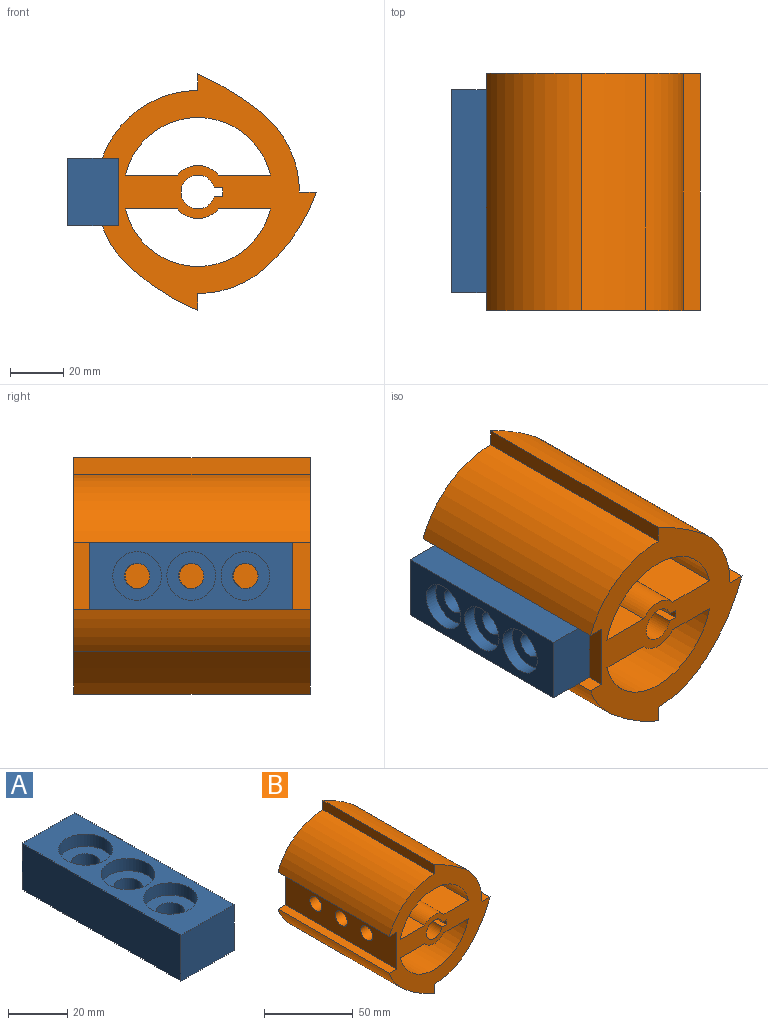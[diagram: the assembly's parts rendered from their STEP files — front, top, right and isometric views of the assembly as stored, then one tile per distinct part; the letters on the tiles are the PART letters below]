
ASSEMBLY  parts=2 mates=1
PART A: 15 faces, bbox 25.4x76.2x19.1 mm
  f0: cylinder r=4.76mm len=13.97mm, axis (0,0,1), area 418mm2, adj f5,f14
  f1: cylinder r=4.76mm len=13.97mm, axis (0,0,1), area 418mm2, adj f5,f12
  f2: cylinder r=4.76mm len=13.97mm, axis (0,0,1), area 418mm2, adj f5,f10
  f3: plane 76.2x25.4mm, normal (0,0,1), area 1147.4mm2, adj f4,f6,f7,f8,f9,f11,f13
  f4: plane 76.2x19.05mm, normal (-1,0,0), area 1451.6mm2, adj f3,f5,f7,f8
  f5: plane 76.2x25.4mm, normal (0,0,-1), area 1721.7mm2, adj f0,f1,f2,f4,f6,f7,f8
  f6: plane 76.2x19.05mm, normal (1,0,0), area 1451.6mm2, adj f3,f5,f7,f8
  f7: plane 25.4x19.05mm, normal (0,1,0), area 483.9mm2, adj f3,f4,f5,f6
  f8: plane 25.4x19.05mm, normal (0,-1,0), area 483.9mm2, adj f3,f4,f5,f6
  f9: cylinder r=9.14mm len=18.29mm, axis (0,0,1), area 291.9mm2, adj f3,f10
  f10: plane 18.29x18.29mm, normal (0,0,1), area 191.4mm2, adj f2,f9
  f11: cylinder r=9.14mm len=18.29mm, axis (0,0,1), area 291.9mm2, adj f3,f12
  f12: plane 18.29x18.29mm, normal (0,0,1), area 191.4mm2, adj f1,f11
  f13: cylinder r=9.14mm len=18.29mm, axis (0,0,1), area 291.9mm2, adj f3,f14
  f14: plane 18.29x18.29mm, normal (0,0,1), area 191.4mm2, adj f0,f13
PART B: 33 faces, bbox 80.4x88.9x88.9 mm
  f0: cylinder r=38.1mm len=88.9mm, axis (0,1,0), area 1702.8mm2, adj f1,f2,f14,f24
  f1: plane 88.9x80.37mm, normal (0,-1,0), area 2746.6mm2, adj f0,f3,f4,f5,f6,f7,f8,f9
  f2: plane 88.9x80.37mm, normal (0,1,0), area 2746.6mm2, adj f0,f3,f4,f5,f6,f7,f8,f9
  f3: cylinder r=6.35mm len=88.9mm, axis (0,1,0), area 3261.7mm2, adj f1,f2,f4,f23
  f4: plane 88.9x3.24mm, normal (0,0,-1), area 288.3mm2, adj f1,f2,f3,f5
  f5: plane 88.9x3.18mm, normal (-1,0,0), area 282.3mm2, adj f1,f2,f4,f23
  f6: cylinder r=9.97mm len=88.9mm, axis (0,1,0), area 1561.5mm2, adj f1,f2,f7,f20
  f7: plane 88.9x19.52mm, normal (0,0,-1), area 1735.2mm2, adj f1,f2,f6,f8
  f8: cylinder r=27.94mm len=88.9mm, axis (0,1,0), area 6664.3mm2, adj f1,f2,f7,f20
  f9: plane 88.9x19.52mm, normal (0,0,1), area 1735.2mm2, adj f1,f2,f10,f21
  f10: cylinder r=9.97mm len=88.9mm, axis (0,1,0), area 1561.5mm2, adj f1,f2,f9,f11
  f11: plane 88.9x19.52mm, normal (0,0,1), area 1735.2mm2, adj f1,f2,f10,f21
  f12: plane 88.9x6.35mm, normal (-1,0,0), area 564.5mm2, adj f1,f2,f13,f22
  f13: cylinder r=38.1mm len=88.9mm, axis (0,1,0), area 4169.4mm2, adj f1,f2,f12,f26
  f14: cylinder r=91.33mm len=88.9mm, axis (0,1,0), area 2678.3mm2, adj f0,f1,f2,f15
  f15: plane 88.9x6.35mm, normal (1,0,0), area 564.5mm2, adj f1,f2,f14,f16
  f16: cylinder r=38.1mm len=88.9mm, axis (0,1,0), area 2429.9mm2, adj f1,f2,f15,f17
  f17: cylinder r=67.63mm len=88.9mm, axis (0,1,0), area 3115.1mm2, adj f1,f2,f16,f18
  f18: plane 88.9x6.35mm, normal (0,0,1), area 564.5mm2, adj f1,f2,f17,f19
  f19: cylinder r=38.1mm len=88.9mm, axis (0,1,0), area 3045.6mm2, adj f1,f2,f18,f22
  f20: plane 88.9x19.52mm, normal (0,0,-1), area 1735.2mm2, adj f1,f2,f6,f8
  f21: cylinder r=27.94mm len=88.9mm, axis (0,1,0), area 6664.3mm2, adj f1,f2,f9,f11
  f22: cylinder r=117.44mm len=88.9mm, axis (0,1,0), area 2482.2mm2, adj f1,f2,f12,f19
  f23: plane 88.9x3.24mm, normal (0,0,1), area 288.3mm2, adj f1,f2,f3,f5
  f24: plane 88.9x6.08mm, normal (0,0,1), area 540.2mm2, adj f0,f1,f2,f25
  f25: plane 88.9x25.4mm, normal (-1,0,0), area 2044.3mm2, adj f1,f2,f24,f26,f27,f29,f31
  f26: plane 88.9x6.08mm, normal (0,0,-1), area 540.2mm2, adj f1,f2,f13,f25
  f27: cylinder r=4.76mm len=12.7mm, axis (-1,0,0), area 380mm2, adj f25,f28
  f28: plane 9.53x9.53mm, normal (-1,0,0), area 71.3mm2, adj f27
  f29: cylinder r=4.76mm len=12.7mm, axis (-1,0,0), area 380mm2, adj f25,f30
  f30: plane 9.53x9.53mm, normal (-1,0,0), area 71.3mm2, adj f29
  f31: cylinder r=4.76mm len=12.7mm, axis (-1,0,0), area 380mm2, adj f25,f32
  f32: plane 9.53x9.53mm, normal (-1,0,0), area 71.3mm2, adj f31
PLACE A rot(axis=(0,-1,0),90deg) t=(10.24,-4.81,-23.12)mm
PLACE B t=(49.61,77.45,-23.12)mm
MATE planar A.f1 <-> B.f31  axis (1,0,0) through (19.77,53.61,-23.12)mm
